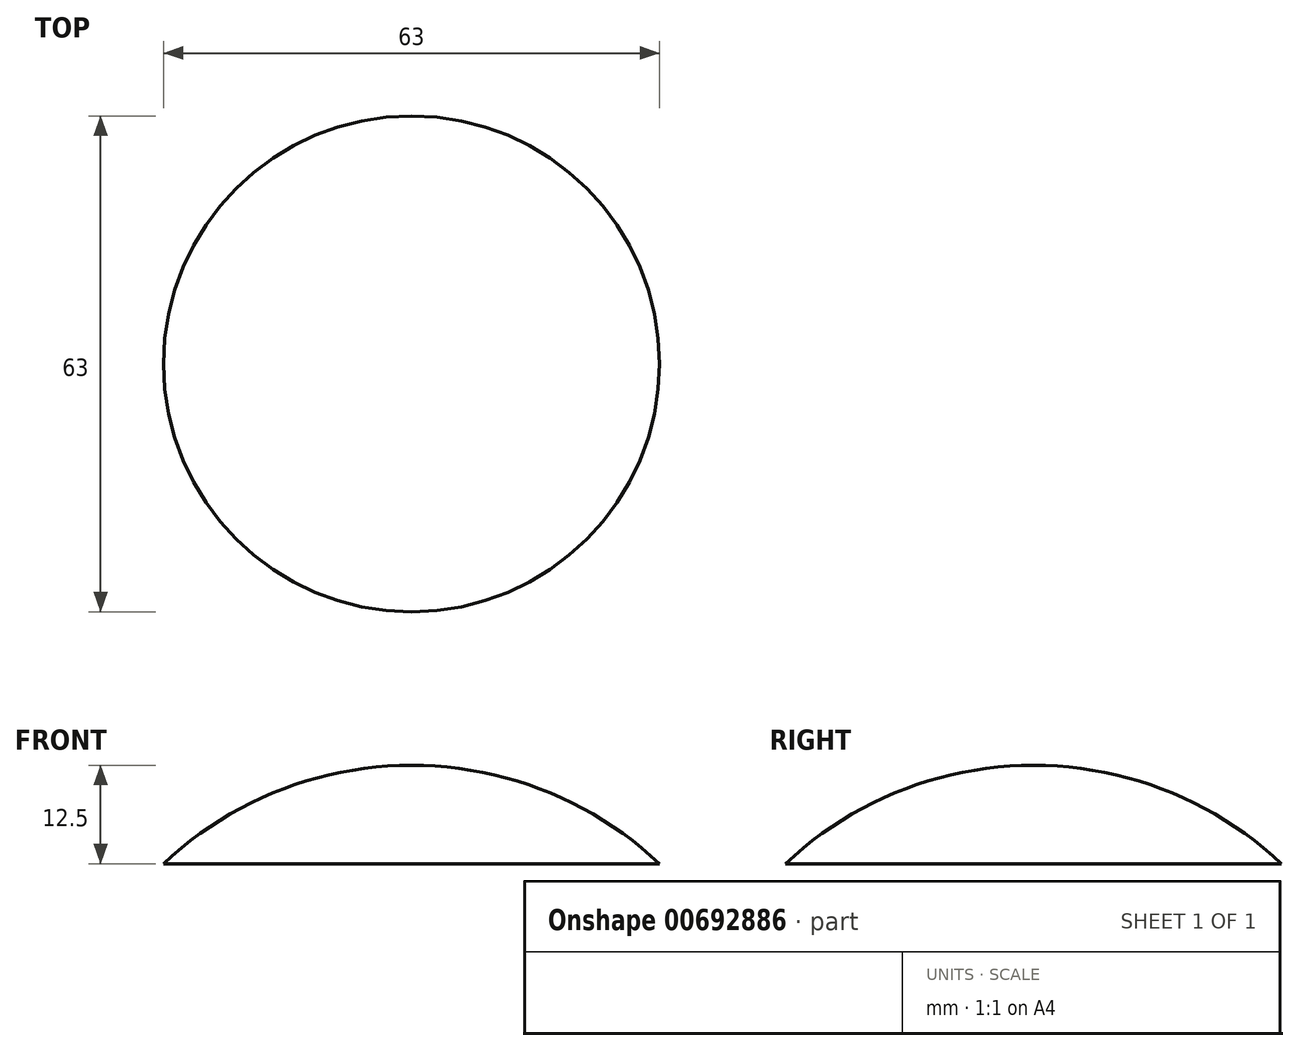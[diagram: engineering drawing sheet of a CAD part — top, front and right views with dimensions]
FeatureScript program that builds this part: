
annotation { "Feature Type Name" : "Feature", "Feature Type Description" : "" }
export const myFeature = defineFeature(function(context is Context, id is Id, definition is map)
    precondition{}
    {
        {
            var Q0;
            Q0=qCreatedBy(makeId("Front.planeOp"),FACE);
            var sketch = newSketch(context, id + "F0", { "sketchPlane" : qUnion([Q0])});
            skPoint(sketch, "E0", {"position": v(0, 50) * mm});
            skArc(sketch, "E1", {"start": v(0, 50) * mm, "mid": v(-16.94, 46.76) * mm, "end": v(-31.5, 37.5) * mm});
            skLineSegment(sketch, "E2", {"start": v(0, 0) * mm, "end": v(0, -29.82) * mm});
            skLineSegment(sketch, "E3", {"start": v(-31.5, 37.5) * mm, "end": v(0, 37.5) * mm});
            skLineSegment(sketch, "E4", {"start": v(0, 37.5) * mm, "end": v(0, 50) * mm});
            skLineSegment(sketch, "E5", {"start": v(0, 37.5) * mm, "end": v(0, 20.94) * mm});
            skSolve(sketch);
        }
        {
            var Q0;
            Q0=qSketchRegion(id+"F0",true);
            var Q1;
            Q1=sQuery(id+"F0.wireOp",EDGE,"E2");
            revolve(context, id + "F1", {"entities" : qUnion([Q0]), "axis" : qUnion([Q1]), "revolveType" : RevolveType.FULL});
        }
    });
